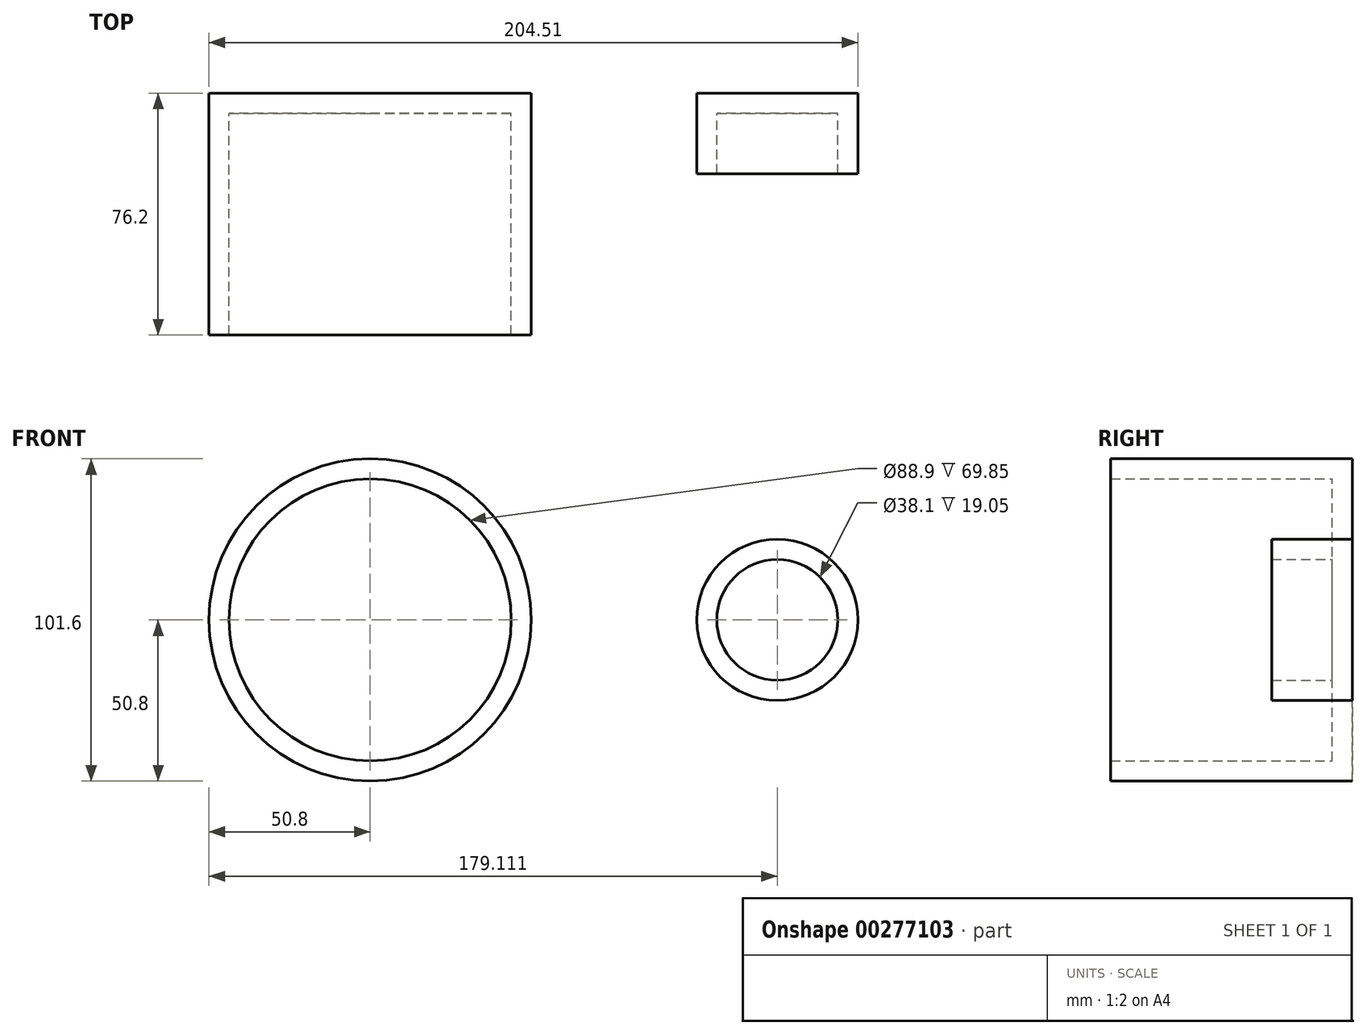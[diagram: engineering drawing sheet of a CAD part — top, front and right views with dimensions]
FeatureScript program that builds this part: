
annotation { "Feature Type Name" : "Feature", "Feature Type Description" : "" }
export const myFeature = defineFeature(function(context is Context, id is Id, definition is map)
    precondition{}
    {
        {
            var Q0;
            Q0=qCreatedBy(makeId("Front.planeOp"),FACE);
            var sketch = newSketch(context, id + "F0", { "sketchPlane" : qUnion([Q0])});
            skCircle(sketch, "E0", {"center": v(-52.9, 0) * mm, "radius": 50.8 * mm});
            skCircle(sketch, "E1", {"center": v(75.4, 0) * mm, "radius": 25.4 * mm});
            skSolve(sketch);
        }
        {
            var Q0;
            Q0=makeQuery(id+"F0.imprint","IMPRINT",FACE,{"disambiguationData":[TD([[makeQuery(id+"F0.imprint","IMPRINT",EDGE,{"derivedFrom":sQuery(id+"F0.wireOp",EDGE,"E1")}),1.0]])]});
            extrude(context, id + "F1", {"entities" : qUnion([Q0]), "depth" : 25.4 * mm});
        }
        {
            var Q0;
            Q0=makeQuery(id+"F0.imprint","IMPRINT",FACE,{"disambiguationData":[TD([[makeQuery(id+"F0.imprint","IMPRINT",EDGE,{"derivedFrom":sQuery(id+"F0.wireOp",EDGE,"E0")}),1.0]])]});
            extrude(context, id + "F2", {"entities" : qUnion([Q0]), "depth" : 76.2 * mm});
        }
        {
            var Q0;
            Q0=makeQuery(id+"F2.opExtrude","CAP_FACE",FACE,{"disambiguationData":[OSD([sQuery(id+"F0.wireOp",EDGE,"E0")])],"isStart":false});
            var Q1;
            Q1=makeQuery(id+"F1.opExtrude","CAP_FACE",FACE,{"disambiguationData":[OSD([sQuery(id+"F0.wireOp",EDGE,"E1")])],"isStart":false});
            shell(context, id + "F3", {"entities" : qUnion([Q0, Q1]), "thickness" : 6.35 * mm});
        }
    });
